# Revit family: Window_Curtain_Wall-Casement_Outswing-Kawneer-AA4325
name_source: partatom
category: Windows
revit_build: Autodesk Revit 2015 (Build: 20140905_0730(x64)
units: mm (PartAtom-declared; Revit-internal decimal feet)

## types (1)
- AA4325 - Outswing - Active
    Assembly Code = B2020110
    CTRL Active Head Visibility = Yes
    CTRL Center Mullion Visiblility = No
    CTRL Configuration Number = 1
    CTRL Panel Active Frame Width = 0' - 2 11/32"
    Center Mullion Width = 0' - 3 1/4"
    Depth = 0' - 3 1/4"
    Description = Casement Outswing Window
    Fixed Jamb Width = 0' - 2 1/4"
    Frame Material = Metal - Kawneer - Aluminum
    Glazing Material = Glass - Kawneer - Clear
    Head Width = 0' - 3 3/8"
    Height Maximum = 5' - 0"
    Height Minimum = 1' - 5"
    Jamb Width = 0' - 3 3/8"
    Manufacturer = Kawneer
    Model = AA 4325
    Panel Configuration = X
    Product data url = https://bimobject.com
    Sill Width = 0' - 3 3/8"
    URL = http://www.kawneer.com
    Width Maximum = 10' - 0"
    Width Minimum = 1' - 0"

## geometry (parser evidence)
native form markers: Blend x6, Sweep x1
no freeform markers — native parametric forms only
